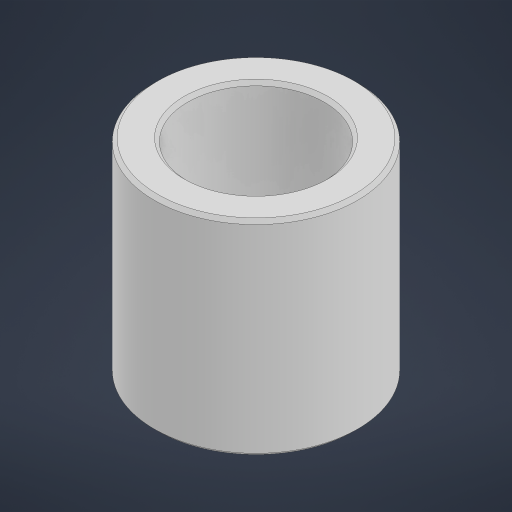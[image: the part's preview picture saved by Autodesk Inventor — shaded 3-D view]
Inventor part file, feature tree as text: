
AUTODESK INVENTOR PART (.ipt)
format: ipt  version: 2023 (Build 270158000, 158)  size: 172,544 bytes
history: native  units: in
note: dims shown in document units (in); Inventor stores cm internally (conversion verified against a paired STEP export)
features: chamfer x1
ambient origin geometry x8: Origin, YZ Plane, XZ Plane, XY Plane, X Axis, Y Axis, Z Axis, Center Point
bodies: Solid1 (feature_tree)
feature tree (1):
  chamfer  "Chamfer1"  [1 undecoded]
note: 1 required parameter value undecoded (feature->parameter linkage not recoverable at this tier; creation-order binding heuristic only, values carry confidence <= 0.55)
